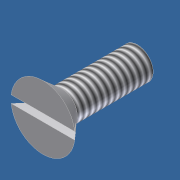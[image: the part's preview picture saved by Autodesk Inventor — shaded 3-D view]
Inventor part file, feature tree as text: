
AUTODESK INVENTOR PART (.ipt)
format: ipt  version: unknown  size: 186,880 bytes
history: native  units: in
note: dims shown in document units (in); Inventor stores cm internally (conversion verified against a paired STEP export)
features: sketch x2, revolve x1, thread x1, extrude x1
ambient origin geometry x8: Origin, YZ Plane, XZ Plane, XY Plane, X Axis, Y Axis, Z Axis, Center Point
bodies: Solid1 (feature_tree)
feature tree (5):
  revolve  "Revolution1"  [1 undecoded]
  thread  "Thread1"  [1 undecoded]
  extrude  "Extrusion2"  TaperAngle=90.0deg  [1 undecoded]
  sketch  "Sketch1"  dims[d0=0.2535in d1=0.125in d2=0.75in]
  sketch  "Sketch4"  dims[d3=0.2817in d4=90.0deg d5=1.0in d6=0.0in d12=0.03in d13=0.03in d14=0.06in d15=0.0in]
note: 3 required parameter values undecoded (feature->parameter linkage not recoverable at this tier; creation-order binding heuristic only, values carry confidence <= 0.55)